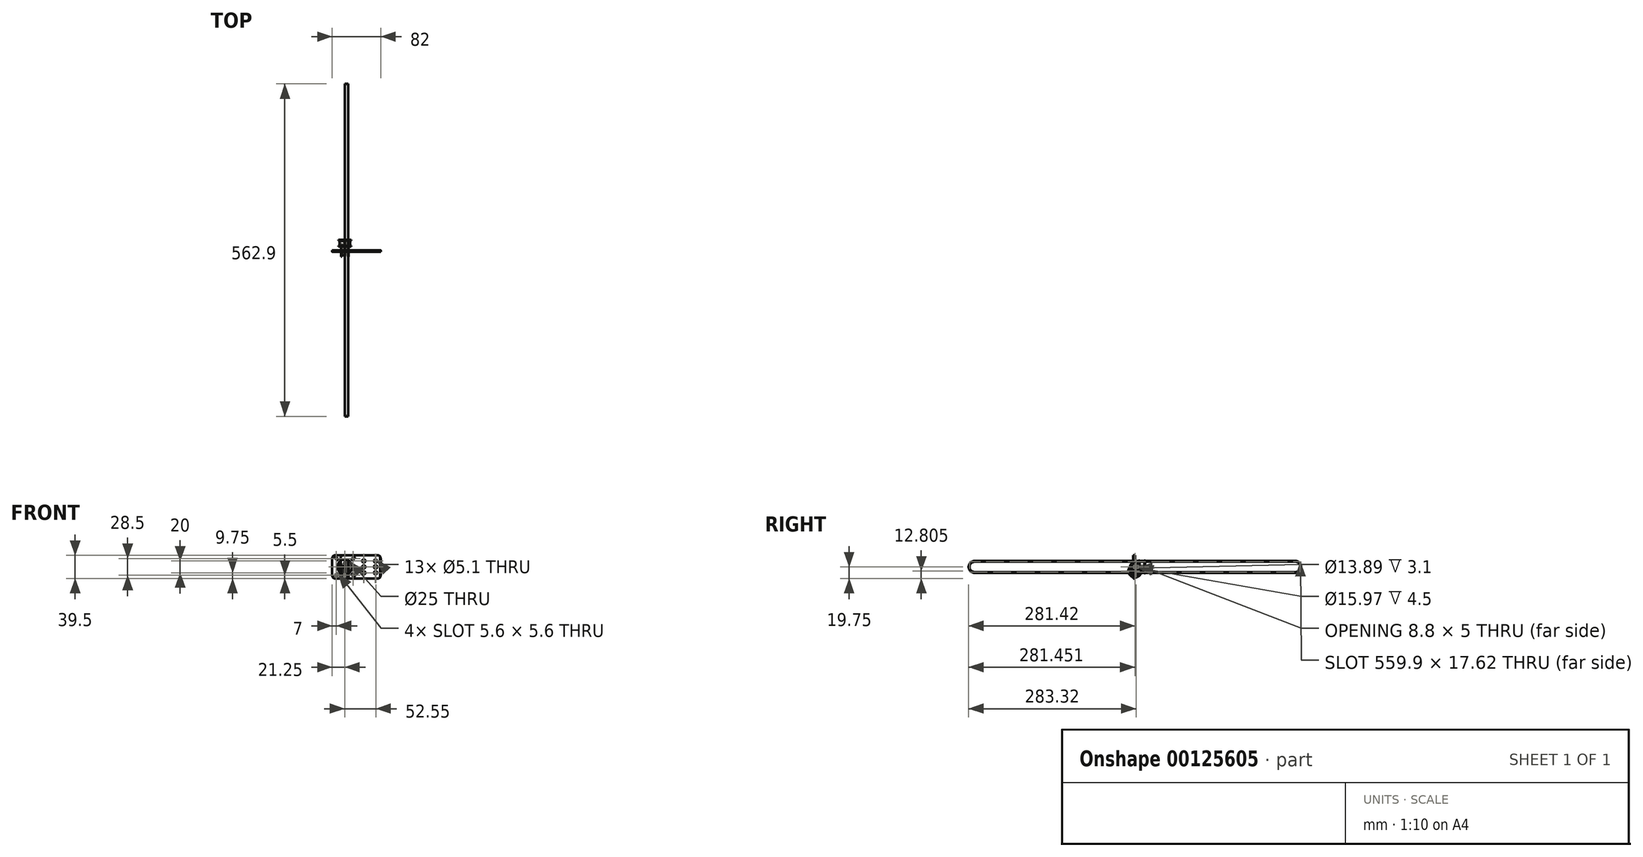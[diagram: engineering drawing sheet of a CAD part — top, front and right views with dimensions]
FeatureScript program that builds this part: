
annotation { "Feature Type Name" : "Feature", "Feature Type Description" : "" }
export const myFeature = defineFeature(function(context is Context, id is Id, definition is map)
    precondition{}
    {
        {
            var Q0;
            Q0=qCreatedBy(makeId("Front.planeOp"),FACE);
            var sketch = newSketch(context, id + "F0", { "sketchPlane" : qUnion([Q0])});
            skCircle(sketch, "E0", {"center": v(0, 0) * mm, "radius": 12.5 * mm});
            skLineSegment(sketch, "E1.bottom", {"start": v(-16.25, 19.75) * mm, "end": v(55.75, 19.75) * mm});
            skLineSegment(sketch, "E1.top", {"start": v(-16.25, -19.75) * mm, "end": v(55.75, -19.75) * mm});
            skLineSegment(sketch, "E1.left", {"start": v(-21.25, 14.75) * mm, "end": v(-21.25, -14.75) * mm});
            skLineSegment(sketch, "E1.right", {"start": v(60.75, 14.75) * mm, "end": v(60.75, -14.75) * mm});
            skLineSegment(sketch, "E2", {"start": v(-15.5, 15.5) * mm, "end": v(-13, 13) * mm, "construction": true});
            skArc(sketch, "E3.0.startCap", {"start": v(-16.6, 14.4) * mm, "mid": v(-16.6, 16.6) * mm, "end": v(-14.4, 16.6) * mm});
            skArc(sketch, "E3.0.endCap", {"start": v(-11.9, 14.1) * mm, "mid": v(-11.9, 11.9) * mm, "end": v(-14.1, 11.9) * mm});
            skLineSegment(sketch, "E3.0.left", {"start": v(-14.4, 16.6) * mm, "end": v(-11.9, 14.1) * mm});
            skLineSegment(sketch, "E3.0.right", {"start": v(-16.6, 14.4) * mm, "end": v(-14.1, 11.9) * mm});
            skLineSegment(sketch, "E4.1.0", {"start": v(-16.6, -14.4) * mm, "end": v(-14.1, -11.9) * mm});
            skArc(sketch, "E4.1.1", {"start": v(-14.1, -11.9) * mm, "mid": v(-11.9, -11.9) * mm, "end": v(-11.9, -14.1) * mm});
            skLineSegment(sketch, "E4.1.2", {"start": v(-15.5, -15.5) * mm, "end": v(-13, -13) * mm});
            skLineSegment(sketch, "E4.1.3", {"start": v(-14.4, -16.6) * mm, "end": v(-11.9, -14.1) * mm});
            skArc(sketch, "E4.1.4", {"start": v(-14.4, -16.6) * mm, "mid": v(-16.6, -16.6) * mm, "end": v(-16.6, -14.4) * mm});
            skLineSegment(sketch, "E4.2.0", {"start": v(14.4, -16.6) * mm, "end": v(11.9, -14.1) * mm});
            skArc(sketch, "E4.2.1", {"start": v(11.9, -14.1) * mm, "mid": v(11.9, -11.9) * mm, "end": v(14.1, -11.9) * mm});
            skLineSegment(sketch, "E4.2.2", {"start": v(15.5, -15.5) * mm, "end": v(13, -13) * mm});
            skLineSegment(sketch, "E4.2.3", {"start": v(16.6, -14.4) * mm, "end": v(14.1, -11.9) * mm});
            skArc(sketch, "E4.2.4", {"start": v(16.6, -14.4) * mm, "mid": v(16.6, -16.6) * mm, "end": v(14.4, -16.6) * mm});
            skLineSegment(sketch, "E4.3.0", {"start": v(16.6, 14.4) * mm, "end": v(14.1, 11.9) * mm});
            skArc(sketch, "E4.3.1", {"start": v(14.1, 11.9) * mm, "mid": v(11.9, 11.9) * mm, "end": v(11.9, 14.1) * mm});
            skLineSegment(sketch, "E4.3.2", {"start": v(15.5, 15.5) * mm, "end": v(13, 13) * mm, "construction": true});
            skLineSegment(sketch, "E4.3.3", {"start": v(14.4, 16.6) * mm, "end": v(11.9, 14.1) * mm});
            skArc(sketch, "E4.3.4", {"start": v(14.4, 16.6) * mm, "mid": v(16.6, 16.6) * mm, "end": v(16.6, 14.4) * mm});
            skCircle(sketch, "E5", {"center": v(32.55, -10) * mm, "radius": 2.55 * mm});
            skCircle(sketch, "E6.0.1.0", {"center": v(32.55, 0) * mm, "radius": 2.55 * mm});
            skCircle(sketch, "E6.0.2.0", {"center": v(32.55, 10) * mm, "radius": 2.55 * mm});
            skCircle(sketch, "E6.1.0.0", {"center": v(52.55, -10) * mm, "radius": 2.55 * mm});
            skCircle(sketch, "E6.1.1.0", {"center": v(52.55, 0) * mm, "radius": 2.55 * mm});
            skCircle(sketch, "E6.1.2.0", {"center": v(52.55, 10) * mm, "radius": 2.55 * mm});
            skLineSegment(sketch, "E6.direction1", {"start": v(32.55, -10) * mm, "end": v(52.55, -10) * mm, "construction": true});
            skLineSegment(sketch, "E6.direction2", {"start": v(32.55, -10) * mm, "end": v(32.55, 0) * mm, "construction": true});
            skPoint(sketch, "E7.visualSharp", {"position": v(-21.25, 19.75) * mm});
            skArc(sketch, "E7.filletArc", {"start": v(-16.25, 19.75) * mm, "mid": v(-19.79, 18.29) * mm, "end": v(-21.25, 14.75) * mm});
            skPoint(sketch, "E8.visualSharp", {"position": v(-21.25, -19.75) * mm});
            skArc(sketch, "E8.filletArc", {"start": v(-21.25, -14.75) * mm, "mid": v(-19.79, -18.29) * mm, "end": v(-16.25, -19.75) * mm});
            skPoint(sketch, "E9.visualSharp", {"position": v(60.75, -19.75) * mm});
            skArc(sketch, "E9.filletArc", {"start": v(55.75, -19.75) * mm, "mid": v(59.29, -18.29) * mm, "end": v(60.75, -14.75) * mm});
            skPoint(sketch, "E10.visualSharp", {"position": v(60.75, 19.75) * mm});
            skArc(sketch, "E10.filletArc", {"start": v(60.75, 14.75) * mm, "mid": v(59.29, 18.29) * mm, "end": v(55.75, 19.75) * mm});
            skLineSegment(sketch, "E11", {"start": v(-13, 13) * mm, "end": v(13, -13) * mm, "construction": true});
            skPoint(sketch, "E12", {"position": v(-14.25, 14.25) * mm});
            skPoint(sketch, "E13", {"position": v(14.25, -14.25) * mm});
            skSolve(sketch);
        }
        {
            var Q0;
            Q0=makeQuery(id+"F0.imprint","IMPRINT",FACE,{"disambiguationData":[TD([[makeQuery(id+"F0.imprint","IMPRINT",EDGE,{"derivedFrom":sQuery(id+"F0.wireOp",EDGE,"E0")}),-1.0]])]});
            extrude(context, id + "F1", {"entities" : qUnion([Q0]), "depth" : 3 * mm});
        }
        {
            var Q0;
            Q0=qCreatedBy(makeId("Front.planeOp"),FACE);
            var sketch = newSketch(context, id + "F2", { "sketchPlane" : qUnion([Q0])});
            skCircle(sketch, "E14", {"center": v(0, 0) * mm, "radius": 2.55 * mm});
            skLineSegment(sketch, "E15.bottom", {"start": v(-2, 19.75) * mm, "end": v(55, 19.75) * mm});
            skLineSegment(sketch, "E15.top", {"start": v(-2, -19.75) * mm, "end": v(55, -19.75) * mm});
            skLineSegment(sketch, "E15.left", {"start": v(-7, 14.75) * mm, "end": v(-7, -14.75) * mm});
            skLineSegment(sketch, "E15.right", {"start": v(60, 14.75) * mm, "end": v(60, -14.75) * mm});
            skCircle(sketch, "E16", {"center": v(31.79, -10) * mm, "radius": 2.55 * mm});
            skCircle(sketch, "E17.0.1.0", {"center": v(31.79, 0) * mm, "radius": 2.55 * mm});
            skCircle(sketch, "E17.0.2.0", {"center": v(31.79, 10) * mm, "radius": 2.55 * mm});
            skCircle(sketch, "E17.1.0.0", {"center": v(51.8, -10) * mm, "radius": 2.55 * mm});
            skCircle(sketch, "E17.1.1.0", {"center": v(51.8, 0) * mm, "radius": 2.55 * mm});
            skCircle(sketch, "E17.1.2.0", {"center": v(51.8, 10) * mm, "radius": 2.55 * mm});
            skLineSegment(sketch, "E17.direction1", {"start": v(31.79, -10) * mm, "end": v(51.8, -10) * mm, "construction": true});
            skLineSegment(sketch, "E17.direction2", {"start": v(31.79, -10) * mm, "end": v(31.79, 0) * mm, "construction": true});
            skPoint(sketch, "E18.visualSharp", {"position": v(-7, 19.75) * mm});
            skArc(sketch, "E18.filletArc", {"start": v(-2, 19.75) * mm, "mid": v(-5.54, 18.29) * mm, "end": v(-7, 14.75) * mm});
            skPoint(sketch, "E19.visualSharp", {"position": v(60, 19.75) * mm});
            skArc(sketch, "E19.filletArc", {"start": v(60, 14.75) * mm, "mid": v(58.54, 18.29) * mm, "end": v(55, 19.75) * mm});
            skPoint(sketch, "E20.visualSharp", {"position": v(60, -19.75) * mm});
            skArc(sketch, "E20.filletArc", {"start": v(55, -19.75) * mm, "mid": v(58.54, -18.29) * mm, "end": v(60, -14.75) * mm});
            skPoint(sketch, "E21.visualSharp", {"position": v(-7, -19.75) * mm});
            skArc(sketch, "E21.filletArc", {"start": v(-7, -14.75) * mm, "mid": v(-5.54, -18.29) * mm, "end": v(-2, -19.75) * mm});
            skSolve(sketch);
        }
        {
            var Q0;
            Q0=makeQuery(id+"F2.imprint","IMPRINT",FACE,{"disambiguationData":[TD([[makeQuery(id+"F2.imprint","IMPRINT",EDGE,{"derivedFrom":sQuery(id+"F2.wireOp",EDGE,"E14")}),-1.0]])]});
            extrude(context, id + "F3", {"entities" : qUnion([Q0]), "depth" : 3 * mm});
        }
        {
            var Q0;
            Q0=qCreatedBy(makeId("Front.planeOp"),FACE);
            var sketch = newSketch(context, id + "F4", { "sketchPlane" : qUnion([Q0])});
            skLineSegment(sketch, "E22", {"start": v(-6.35, 1.04) * mm, "end": v(-6.35, 4.05) * mm});
            skLineSegment(sketch, "E23", {"start": v(-6.35, 4.05) * mm, "end": v(-4.75, 4.05) * mm});
            skLineSegment(sketch, "E24", {"start": v(-4.75, 4.06) * mm, "end": v(-4.75, 1.8) * mm});
            skLineSegment(sketch, "E25", {"start": v(-4.75, 1.8) * mm, "end": v(4.75, 1.8) * mm});
            skLineSegment(sketch, "E26", {"start": v(4.75, 1.8) * mm, "end": v(4.75, 4.06) * mm});
            skLineSegment(sketch, "E27", {"start": v(4.75, 4.06) * mm, "end": v(6.35, 4.06) * mm});
            skLineSegment(sketch, "E28", {"start": v(6.35, 4.05) * mm, "end": v(6.35, 1.04) * mm});
            skLineSegment(sketch, "E29", {"start": v(6.35, 1.04) * mm, "end": v(1.55, 1.04) * mm});
            skLineSegment(sketch, "E30", {"start": v(1.55, 1.04) * mm, "end": v(1.55, 0) * mm});
            skLineSegment(sketch, "E31", {"start": v(1.55, 0) * mm, "end": v(-1.55, 0) * mm});
            skLineSegment(sketch, "E32", {"start": v(-1.55, 0) * mm, "end": v(-1.55, 1.04) * mm});
            skLineSegment(sketch, "E33", {"start": v(-1.55, 1.04) * mm, "end": v(-6.35, 1.04) * mm});
            skLineSegment(sketch, "E34", {"start": v(0, 0) * mm, "end": v(0, 1.8) * mm, "construction": true});
            skLineSegment(sketch, "E35", {"start": v(-1.55, -6.95) * mm, "end": v(1.55, -6.95) * mm, "construction": true});
            skSolve(sketch);
        }
        {
            var Q0;
            Q0=makeQuery(id+"F4.imprint","IMPRINT",FACE,{"disambiguationData":[TD([[makeQuery(id+"F4.imprint","IMPRINT",EDGE,{"derivedFrom":sQuery(id+"F4.wireOp",EDGE,"E22")}),-1.0]])]});
            var Q1;
            Q1=sQuery(id+"F4.wireOp",EDGE,"E35");
            revolve(context, id + "F5", {"entities" : qUnion([Q0]), "axis" : qUnion([Q1]), "revolveType" : RevolveType.FULL});
        }
        {
            var Q0;
            Q0=makeQuery(id+"F5.opRevolve","SWEPT_EDGE",EDGE,{"disambiguationData":[OSD([sQuery(id+"F4.wireOp",EDGE,"E22"),sQuery(id+"F4.wireOp",EDGE,"E33")])]});
            var Q1;
            Q1=makeQuery(id+"F5.opRevolve","SWEPT_EDGE",EDGE,{"disambiguationData":[OSD([sQuery(id+"F4.wireOp",EDGE,"E28"),sQuery(id+"F4.wireOp",EDGE,"E29")])]});
            chamfer(context, id + "F6", {"entities" : qUnion([Q0, Q1]), "width" : .3 * mm, "tangentPropagation" : true});
        }
        {
            var Q0;
            Q0=qCreatedBy(makeId("Right.planeOp"),FACE);
            var sketch = newSketch(context, id + "F7", { "sketchPlane" : qUnion([Q0])});
            skCircle(sketch, "E36", {"center": v(0, 0) * mm, "radius": 8 * mm});
            skCircle(sketch, "E37", {"center": v(0, 0) * mm, "radius": 2.5 * mm});
            skCircle(sketch, "E38", {"center": v(0, 0) * mm, "radius": 5 * mm});
            skSolve(sketch);
        }
        {
            var Q0;
            Q0 = qSketchRegion(id + "F7", true);
            var Q1;
            Q1=makeQuery(id+"F7.imprint","IMPRINT",FACE,{"disambiguationData":[TD([[makeQuery(id+"F7.imprint","IMPRINT",EDGE,{"derivedFrom":sQuery(id+"F7.wireOp",EDGE,"E37")}),-1.0]])]});
            extrude(context, id + "F8", {"entities" : qUnion([Q0, Q1]), "depth" : 5 * mm});
        }
        {
            var Q0;
            Q0=makeQuery(id+"F8.opExtrude","CAP_EDGE",EDGE,{"disambiguationData":[OSD([sQuery(id+"F7.wireOp",EDGE,"E36")])],"isStart":false});
            var Q1;
            Q1=makeQuery(id+"F8.opExtrude","CAP_EDGE",EDGE,{"disambiguationData":[OSD([sQuery(id+"F7.wireOp",EDGE,"E36")])],"isStart":true});
            chamfer(context, id + "F9", {"entities" : qUnion([Q0, Q1]), "width" : .3 * mm, "tangentPropagation" : true});
        }
        {
            var Q0;
            Q0=makeQuery(id+"F7.imprint","IMPRINT",FACE,{"disambiguationData":[TD([[makeQuery(id+"F7.imprint","IMPRINT",EDGE,{"derivedFrom":sQuery(id+"F7.wireOp",EDGE,"E37")}),-1.0]])]});
            extrude(context, id + "F10", {"entities" : qUnion([Q0]), "depth" : 1 * mm});
        }
        {
            var Q0;
            Q0=qCreatedBy(makeId("Right.planeOp"),FACE);
            var sketch = newSketch(context, id + "F11", { "sketchPlane" : qUnion([Q0])});
            skArc(sketch, "E39", {"start": v(-271.17, 8.75) * mm, "mid": v(-279.92, 0) * mm, "end": v(-271.17, -8.75) * mm});
            skArc(sketch, "E40", {"start": v(271.17, -8.81) * mm, "mid": v(279.98, 0) * mm, "end": v(271.17, 8.81) * mm});
            skLineSegment(sketch, "E41", {"start": v(-271.17, 0) * mm, "end": v(271.17, 0) * mm, "construction": true});
            skLineSegment(sketch, "E42", {"start": v(-271.17, 8.75) * mm, "end": v(271.17, 8.81) * mm});
            skLineSegment(sketch, "E43.MirrorCS", {"start": v(-271.17, -8.75) * mm, "end": v(271.17, -8.81) * mm});
            skLineSegment(sketch, "E44.0", {"start": v(-271.17, 10.25) * mm, "end": v(271.17, 10.31) * mm});
            skArc(sketch, "E44.1", {"start": v(-271.17, 10.25) * mm, "mid": v(-281.42, 0) * mm, "end": v(-271.17, -10.25) * mm});
            skLineSegment(sketch, "E44.2", {"start": v(-271.17, -10.25) * mm, "end": v(271.17, -10.31) * mm});
            skArc(sketch, "E44.3", {"start": v(271.17, -10.31) * mm, "mid": v(281.48, 0) * mm, "end": v(271.17, 10.31) * mm});
            skSolve(sketch);
        }
        {
            var Q0;
            Q0=makeQuery(id+"F11.imprint","IMPRINT",FACE,{"disambiguationData":[TD([[makeQuery(id+"F11.imprint","IMPRINT",EDGE,{"derivedFrom":sQuery(id+"F11.wireOp",EDGE,"E39")}),-1.0]])]});
            extrude(context, id + "F12", {"entities" : qUnion([Q0]), "depth" : 6 * mm});
        }
        {
            var Q0;
            Q0=qCreatedBy(makeId("Right.planeOp"),FACE);
            var sketch = newSketch(context, id + "F13", { "sketchPlane" : qUnion([Q0])});
            skLineSegment(sketch, "E45.bottom", {"start": v(0, 6.5) * mm, "end": v(6.3, 6.5) * mm});
            skLineSegment(sketch, "E45.top", {"start": v(0, -6.5) * mm, "end": v(6.3, -6.5) * mm});
            skLineSegment(sketch, "E45.left", {"start": v(0, 6.5) * mm, "end": v(0, -6.5) * mm});
            skLineSegment(sketch, "E45.right", {"start": v(6.3, 6.5) * mm, "end": v(6.3, -6.5) * mm});
            skLineSegment(sketch, "E46.bottom", {"start": v(6.3, 11) * mm, "end": v(7.66, 11) * mm});
            skLineSegment(sketch, "E46.top", {"start": v(6.3, -11) * mm, "end": v(7.66, -11) * mm});
            skLineSegment(sketch, "E46.left", {"start": v(6.3, 11) * mm, "end": v(6.3, -11) * mm});
            skLineSegment(sketch, "E46.right", {"start": v(17.5, 11) * mm, "end": v(17.5, -11) * mm});
            skLineSegment(sketch, "E47", {"start": v(0, 0) * mm, "end": v(17.5, 0) * mm});
            skPoint(sketch, "E48", {"position": v(6.3, 0) * mm});
            skLineSegment(sketch, "E49", {"start": v(7.66, 11) * mm, "end": v(7.66, -11) * mm});
            skLineSegment(sketch, "E50", {"start": v(11.9, 11) * mm, "end": v(11.9, -11) * mm, "construction": true});
            skLineSegment(sketch, "E51.MirrorCS", {"start": v(16.14, 11) * mm, "end": v(16.14, -11) * mm});
            skLineSegment(sketch, "E52", {"start": v(7.9, 8.81) * mm, "end": v(7.9, -8.81) * mm});
            skLineSegment(sketch, "E53.MirrorCS", {"start": v(15.9, 8.81) * mm, "end": v(15.9, -8.81) * mm});
            skLineSegment(sketch, "E54", {"start": v(7.9, 8.81) * mm, "end": v(15.9, 8.81) * mm});
            skLineSegment(sketch, "E55.MirrorCS", {"start": v(7.9, -8.81) * mm, "end": v(15.9, -8.81) * mm});
            skLineSegment(sketch, "E56.trimOffspring", {"start": v(16.14, 11) * mm, "end": v(17.5, 11) * mm});
            skLineSegment(sketch, "E57.trimOffspring", {"start": v(16.14, -11) * mm, "end": v(17.5, -11) * mm});
            skLineSegment(sketch, "E58", {"start": v(7.66, 11) * mm, "end": v(7.9, 8.81) * mm});
            skLineSegment(sketch, "E59.MirrorCS", {"start": v(16.14, 11) * mm, "end": v(15.9, 8.81) * mm});
            skLineSegment(sketch, "E60.MirrorCS", {"start": v(7.66, -11) * mm, "end": v(7.9, -8.81) * mm});
            skLineSegment(sketch, "E61.MirrorCS", {"start": v(16.14, -11) * mm, "end": v(15.9, -8.81) * mm});
            skPoint(sketch, "E62.orphan", {"position": v(7.9, 11) * mm});
            skPoint(sketch, "E63.orphan", {"position": v(15.9, 11) * mm});
            skPoint(sketch, "E64.orphan", {"position": v(15.9, -11) * mm});
            skPoint(sketch, "E65.orphan", {"position": v(7.9, -11) * mm});
            skCircle(sketch, "E66", {"center": v(3.15, 0) * mm, "radius": 1.5 * mm});
            skPoint(sketch, "E67", {"position": v(3.15, 6.5) * mm});
            skLineSegment(sketch, "E68", {"start": v(0, 2.5) * mm, "end": v(17.5, 2.5) * mm});
            skLineSegment(sketch, "E69.MirrorCS", {"start": v(0, -2.5) * mm, "end": v(17.5, -2.5) * mm});
            skSolve(sketch);
        }
        {
            var Q0;
            {var subQ0=sQuery(id+"F13.wireOp",EDGE,"E45.bottom");Q0=makeQuery(id+"F13.imprint","IMPRINT",FACE,{"disambiguationData":[TD([[makeQuery(id+"F13.imprint","IMPRINT",EDGE,{"derivedFrom":subQ0}),-1.0]])]});}
            var Q1;
            {var subQ6=sQuery(id+"F13.wireOp",EDGE,"E46.bottom");Q1=makeQuery(id+"F13.imprint","IMPRINT",FACE,{"disambiguationData":[TD([[makeQuery(id+"F13.imprint","IMPRINT",EDGE,{"derivedFrom":subQ6}),-1.0]])]});}
            var Q2;
            {var subQ0=sQuery(id+"F13.wireOp",EDGE,"E58");Q2=makeQuery(id+"F13.imprint","IMPRINT",FACE,{"disambiguationData":[TD([[makeQuery(id+"F13.imprint","IMPRINT",EDGE,{"derivedFrom":subQ0}),-1.0]])]});}
            var Q3;
            {var subQ0=sQuery(id+"F13.wireOp",EDGE,"E54");Q3=makeQuery(id+"F13.imprint","IMPRINT",FACE,{"disambiguationData":[TD([[makeQuery(id+"F13.imprint","IMPRINT",EDGE,{"derivedFrom":subQ0}),-1.0]])]});}
            var Q4;
            {var subQ0=sQuery(id+"F13.wireOp",EDGE,"E59.MirrorCS");Q4=makeQuery(id+"F13.imprint","IMPRINT",FACE,{"disambiguationData":[TD([[makeQuery(id+"F13.imprint","IMPRINT",EDGE,{"derivedFrom":subQ0}),1.0]])]});}
            var Q5;
            {var subQ0=sQuery(id+"F13.wireOp",EDGE,"E56.trimOffspring");Q5=makeQuery(id+"F13.imprint","IMPRINT",FACE,{"disambiguationData":[TD([[makeQuery(id+"F13.imprint","IMPRINT",EDGE,{"derivedFrom":subQ0}),-1.0]])]});}
            var Q6;
            Q6=sQuery(id+"F13.wireOp",EDGE,"E47");
            revolve(context, id + "F14", {"entities" : qUnion([Q0, Q1, Q2, Q3, Q4, Q5]), "axis" : qUnion([Q6]), "revolveType" : RevolveType.FULL});
        }
        {
            var Q0;
            {var subQ0=sQuery(id+"F13.wireOp",EDGE,"E66");var subQ1=sQuery(id+"F13.wireOp",EDGE,"E47");var subQ2=makeQuery(id+"F13.imprint","INTERSECT",VERTEX,{"disambiguationData":[OD(0.0)],"derivedFrom":[subQ1,subQ0]});Q0=makeQuery(id+"F13.imprint","IMPRINT",FACE,{"disambiguationData":[TD([[makeQuery(id+"F13.imprint","IMPRINT",EDGE,{"disambiguationData":[TD([[subQ2,-1.0]])],"derivedFrom":subQ1}),-1.0]])]});}
            var Q1;
            {var subQ0=sQuery(id+"F13.wireOp",EDGE,"E66");var subQ1=sQuery(id+"F13.wireOp",EDGE,"E47");var subQ2=makeQuery(id+"F13.imprint","INTERSECT",VERTEX,{"disambiguationData":[OD(0.0)],"derivedFrom":[subQ1,subQ0]});Q1=makeQuery(id+"F13.imprint","IMPRINT",FACE,{"disambiguationData":[TD([[makeQuery(id+"F13.imprint","IMPRINT",EDGE,{"disambiguationData":[TD([[subQ2,-1.0]])],"derivedFrom":subQ1}),1.0]])]});}
            extrude(context, id + "F15", {"entities" : qUnion([Q0, Q1]), "operationType" : NewBodyOperationType.REMOVE, "endBound" : BoundingType.THROUGH_ALL, "depth" : 25 * mm});
        }
    });
